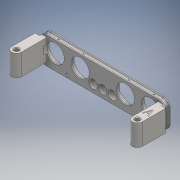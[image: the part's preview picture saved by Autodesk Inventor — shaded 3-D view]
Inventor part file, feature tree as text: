
AUTODESK INVENTOR PART (.ipt)
format: ipt  version: 2016 (Build 200138000, 138)  size: 330,240 bytes
history: native  units: mm
features: extrude x4, chamfer x4, sketch x4
ambient origin geometry x8: Origin, YZ Plane, XZ Plane, XY Plane, X Axis, Y Axis, Z Axis, Center Point
bodies: Solid2 (feature_tree), Solid1 (feature_tree)
feature tree (12):
  extrude  "Extrusion1"  Depth=6.79mm
  chamfer  "Chamfer1"  Distance=4.0mm
  extrude  "Extrusion2"  Depth=2.0mm
  chamfer  "Chamfer2"  Distance=8.5mm
  chamfer  "Chamfer3"  Distance=12.7mm
  chamfer  "Chamfer4"  Distance=3.2mm
  extrude  "Extrusion3"  Depth=2.0mm TaperAngle=0.0deg
  extrude  "Extrusion4"  Depth=2.0mm TaperAngle=30.0deg
  sketch  "Sketch1"  dims[d0=8.5mm d1=6.79mm d3=4.0mm d4=0.0mm]
  sketch  "Sketch2"  dims[d5=2.0mm d6=2.0mm d7=30.0deg d8=8.5mm]
  sketch  "Sketch3"  dims[d9=3.2mm]
  sketch  "Sketch4"  dims[d10=8.5mm d11=8.5mm d12=12.7mm d13=3.2mm d14=4.0mm d15=0.0mm d16=2.0mm d17=2.0mm d18=30.0deg d19=2.0mm d20=2.0mm d21=30.0deg d22=2.0mm d23=2.0mm d24=30.0deg d25=4.0mm d27=24.6mm d28=4.0mm d29=4.0mm d30=4.52mm d31=4.52mm d32=4.0mm d33=0.0mm d34=3.67mm d35=7.15mm d36=1.3mm d37=1.4mm d38=11.7mm d39=5.85mm d40=1.3mm d41=11.7mm d42=5.85mm d43=4.0mm d44=0.0mm]
